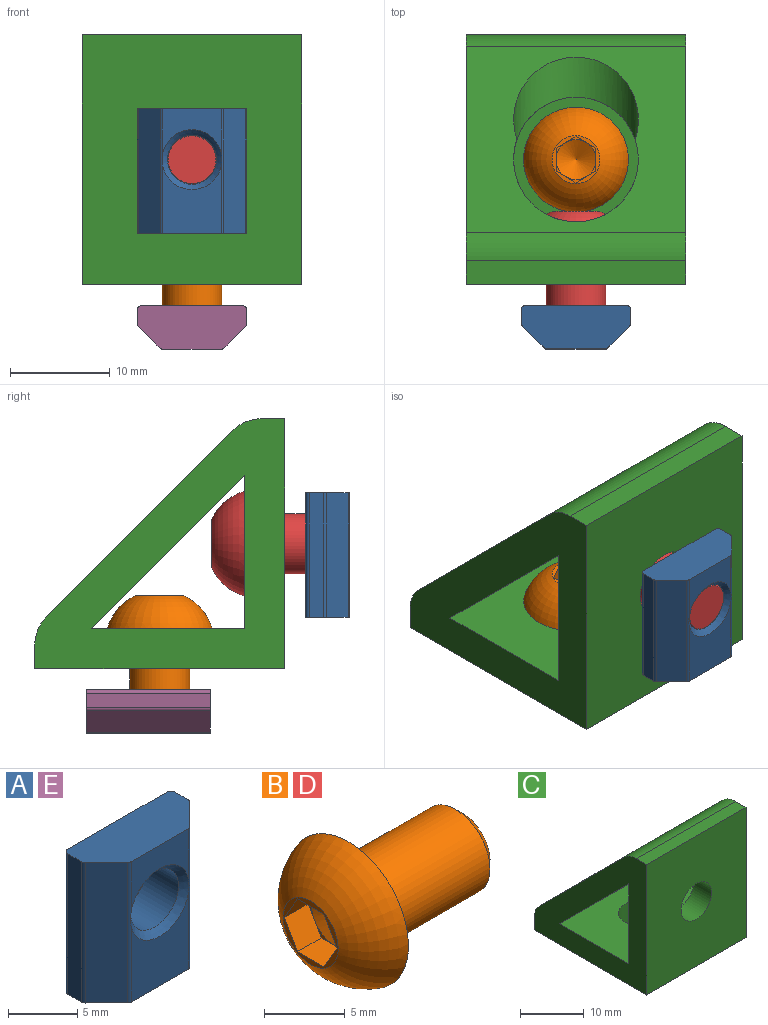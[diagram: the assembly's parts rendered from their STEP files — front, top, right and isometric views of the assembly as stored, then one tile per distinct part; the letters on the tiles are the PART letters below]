
ASSEMBLY  parts=5 mates=4
PART A: 18 faces, bbox 10.9x4.3x12.4 mm
  f0: cylinder r=0.38mm len=12.45mm, axis (0,0,-1), area 3.7mm2, adj f1,f6,f7,f13,f14,f15
  f1: plane 6.71x5.85mm, normal (0,-1,0), area 29mm2, adj f0,f2,f14,f15
  f2: cylinder r=0.38mm len=12.45mm, axis (0,0,-1), area 3.7mm2, adj f1,f7,f8,f13,f14,f15
  f3: cylinder r=0.38mm len=12.45mm, axis (0,0,-1), area 7.4mm2, adj f4,f12,f13,f14
  f4: plane 12.45x1.42mm, normal (-1,0,0), area 17.6mm2, adj f3,f5,f13,f14
  f5: cylinder r=0.38mm len=12.45mm, axis (0,0,-1), area 3.7mm2, adj f4,f6,f13,f14
  f6: plane 12.45x2.17mm, normal (-0.71,-0.71,0), area 38.1mm2, adj f0,f5,f13,f14
  f7: plane 5.85x4.42mm, normal (0,-1,0), area 15.7mm2, adj f0,f2,f13,f15
  f8: plane 12.45x2.17mm, normal (0.71,-0.71,0), area 38.1mm2, adj f2,f9,f13,f14
  f9: cylinder r=0.38mm len=12.45mm, axis (0,0,-1), area 3.7mm2, adj f8,f10,f13,f14
  f10: plane 12.45x1.42mm, normal (1,0,0), area 17.6mm2, adj f9,f11,f13,f14
  f11: cylinder r=0.38mm len=12.45mm, axis (0,0,-1), area 7.4mm2, adj f10,f12,f13,f14
  f12: plane 12.45x10.19mm, normal (0,1,0), area 98.5mm2, adj f3,f11,f13,f14,f16
  f13: plane 10.95x4.34mm, normal (0,0,1), area 41.8mm2, adj f0,f2,f3,f4,f5,f6,f7,f8
  f14: plane 10.95x4.34mm, normal (0,0,-1), area 41.8mm2, adj f0,f1,f2,f3,f4,f5,f6,f8
  f15: cone r=2.46mm half-angle=45deg, axis (0,-1,0), area 13.1mm2, adj f0,f1,f2,f7,f17
  f16: cone r=3mm half-angle=45deg, axis (0,1,0), area 13.1mm2, adj f12,f17
  f17: cylinder r=2.46mm len=4.92mm, axis (0,-1,0), area 50.4mm2, adj f15,f16
PART B: 19 faces, bbox 13.3x10.5x10.5 mm
  f0: plane 4.8x4.8mm, normal (-1,0,0), area 4.2mm2, adj f1,f12,f13,f14,f15,f16,f17
  f1: torus R=0.21mm, axis (1,0,0), area 114.8mm2, adj f0,f2
  f2: plane 10.5x10.5mm, normal (1,0,0), area 58.3mm2, adj f1,f3
  f3: cylinder r=3mm len=9.39mm, axis (1,0,0), area 176.9mm2, adj f2,f4
  f4: cone r=3mm half-angle=45deg, axis (-1,0,0), area 14.7mm2, adj f3,f5
  f5: plane 4.77x4.77mm, normal (1,0,0), area 17.9mm2, adj f4
  f6: plane 1.73x1mm, normal (-1,0,0), area 0.2mm2, adj f14,f15,f18
  f7: plane 2x0.58mm, normal (-1,0,0), area 0.2mm2, adj f13,f14,f18
  f8: plane 1.73x1mm, normal (-1,0,0), area 0.2mm2, adj f12,f13,f18
  f9: plane 1.73x1mm, normal (-1,0,0), area 0.2mm2, adj f12,f17,f18
  f10: plane 2x0.58mm, normal (-1,0,0), area 0.2mm2, adj f16,f17,f18
  f11: plane 1.73x1mm, normal (-1,0,0), area 0.2mm2, adj f15,f16,f18
  f12: plane 2.31x2.08mm, normal (0,0,-1), area 4.8mm2, adj f0,f8,f9,f13,f17
  f13: plane 2.08x2mm, normal (0,0.87,-0.5), area 4.8mm2, adj f0,f7,f8,f12,f14
  f14: plane 2.08x2mm, normal (0,0.87,0.5), area 4.8mm2, adj f0,f6,f7,f13,f15
  f15: plane 2.31x2.08mm, normal (0,0,1), area 4.8mm2, adj f0,f6,f11,f14,f16
  f16: plane 2.08x2mm, normal (0,-0.87,0.5), area 4.8mm2, adj f0,f10,f11,f15,f17
  f17: plane 2.08x2mm, normal (0,-0.87,-0.5), area 4.8mm2, adj f0,f9,f10,f12,f16
  f18: cone r=0mm half-angle=60deg, axis (-1,0,0), area 14.5mm2, adj f6,f7,f8,f9,f10,f11
PART C: 18 faces, bbox 22x25x25 mm
  f0: cylinder r=6.25mm len=12.5mm, axis (0,0,1), area 86.6mm2, adj f10,f16,f17
  f1: cylinder r=4mm len=22mm, axis (-1,0,0), area 69.1mm2, adj f2,f10,f11,f12
  f2: plane 22x2.34mm, normal (0,0,1), area 51.5mm2, adj f1,f3,f11,f12
  f3: plane 25x22mm, normal (0,-1,0), area 513.7mm2, adj f2,f4,f11,f12,f13
  f4: plane 25x22mm, normal (0,0,-1), area 513.7mm2, adj f3,f5,f11,f12,f14
  f5: plane 22x2.34mm, normal (0,1,0), area 51.5mm2, adj f4,f6,f11,f12
  f6: cylinder r=4mm len=22mm, axis (-1,0,0), area 69.1mm2, adj f5,f10,f11,f12
  f7: plane 22x15.34mm, normal (0,-0.71,-0.71), area 274.6mm2, adj f8,f9,f11,f12,f15,f17
  f8: plane 22x15.34mm, normal (0,0,1), area 301.2mm2, adj f7,f9,f11,f12,f14
  f9: plane 22x15.34mm, normal (0,1,0), area 301.2mm2, adj f7,f8,f11,f12,f13
  f10: plane 22x18.66mm, normal (0,0.71,0.71), area 337.4mm2, adj f0,f1,f6,f11,f12,f16
  f11: plane 25x25mm, normal (1,0,0), area 286.1mm2, adj f1,f2,f3,f4,f5,f6,f7,f8
  f12: plane 25x25mm, normal (-1,0,0), area 286.1mm2, adj f1,f2,f3,f4,f5,f6,f7,f8
  f13: cylinder r=3.4mm len=6.8mm, axis (0,-1,0), area 85.5mm2, adj f3,f9
  f14: cylinder r=3.4mm len=6.8mm, axis (0,0,-1), area 85.5mm2, adj f4,f8
  f15: cylinder r=6.25mm len=12.5mm, axis (0,0,1), area 33.9mm2, adj f7,f16,f17
  f16: cylinder r=6.25mm len=12.5mm, axis (0,1,0), area 86.6mm2, adj f0,f10,f15
  f17: cylinder r=6.25mm len=12.5mm, axis (0,1,0), area 33.9mm2, adj f0,f7,f15
PART D: same geometry as B
PART E: same geometry as A
PLACE A t=(0,-6.47,12.5)mm
PLACE B rot(axis=(0,1,0),90deg) t=(0,12.5,4)mm
PLACE C at identity fixed
PLACE D rot(axis=(0.58,-0.58,-0.58),120deg) t=(0,4,12.5)mm
PLACE E rot(axis=(1,0,0),90deg) t=(0,12.5,-6.47)mm
MATE fastened E.f15 <-> C.f0  axis (0,0,1) through (0,12.5,-2.13)mm
MATE fastened B.f1 <-> C.f0  axis (0,0,-1) through (0,12.5,4)mm
MATE fastened A.f15 <-> C.f13  axis (0,1,0) through (0,-2.13,12.5)mm
MATE fastened D.f1 <-> C.f13  axis (0,-1,0) through (0,4,12.5)mm
